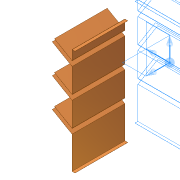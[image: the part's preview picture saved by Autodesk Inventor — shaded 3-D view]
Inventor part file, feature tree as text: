
AUTODESK INVENTOR PART (.ipt)
format: ipt  version: 2012 (Build 160160000, 160)  size: 114,688 bytes
history: native  units: in
note: dims shown in document units (in); Inventor stores cm internally (conversion verified against a paired STEP export)
features: extrude x1, shell x1, sketch x1
ambient origin geometry x8: Origin, YZ Plane, XZ Plane, XY Plane, X Axis, Y Axis, Z Axis, Center Point
bodies: Solid1 (feature_tree)
feature tree (3):
  extrude  "Extrusion1"  Depth=22.0in
  shell  "Shell1"  Thickness=12.0in
  sketch  "Sketch2"  dims[d0=60.0deg d1=22.0in d3=12.0in d4=72.0in d6=3.0in d7=2.0in d8=62.0in d10=42.0in d11=36.0in d12=0.0in d13=0.0625in]
